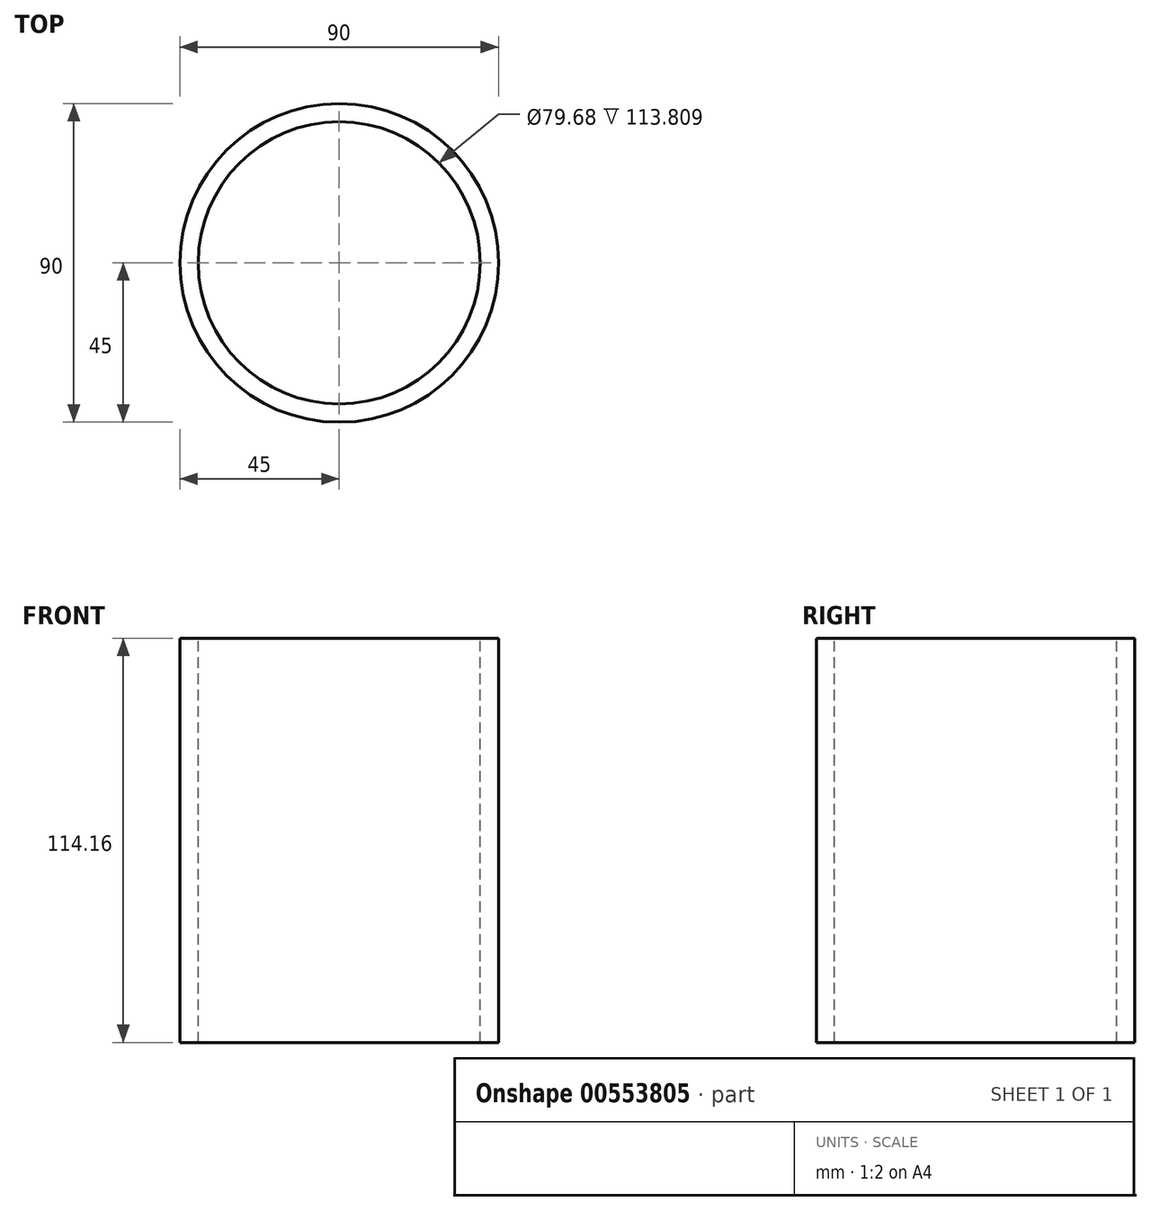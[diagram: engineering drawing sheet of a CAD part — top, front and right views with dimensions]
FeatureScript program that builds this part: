
annotation { "Feature Type Name" : "Feature", "Feature Type Description" : "" }
export const myFeature = defineFeature(function(context is Context, id is Id, definition is map)
    precondition{}
    {
        {
            var Q0;
            Q0=qCreatedBy(makeId("Front.planeOp"),FACE);
            var sketch = newSketch(context, id + "F0", { "sketchPlane" : qUnion([Q0])});
            skLineSegment(sketch, "E0", {"start": v(0, 32.92) * mm, "end": v(0, -87.08) * mm});
            skLineSegment(sketch, "E1", {"start": v(-70, -27.08) * mm, "end": v(70, -27.08) * mm});
            skLineSegment(sketch, "E2", {"start": v(-39.84, -27.08) * mm, "end": v(-39.84, 86.73) * mm});
            skLineSegment(sketch, "E3", {"start": v(-45, 86.73) * mm, "end": v(-45, -27.08) * mm});
            skLineSegment(sketch, "E4", {"start": v(-44.65, 87.08) * mm, "end": v(-40.2, 87.08) * mm});
            skArc(sketch, "E5", {"start": v(-44.65, 87.08) * mm, "mid": v(-44.9, 86.98) * mm, "end": v(-45, 86.73) * mm});
            skArc(sketch, "E6", {"start": v(-39.84, 86.73) * mm, "mid": v(-39.94, 86.98) * mm, "end": v(-40.2, 87.08) * mm});
            skLineSegment(sketch, "E7", {"start": v(-45, -27.08) * mm, "end": v(-39.84, -27.08) * mm});
            skSolve(sketch);
        }
        {
            var Q0;
            Q0=makeQuery(id+"F0.imprint","IMPRINT",FACE,{"disambiguationData":[TD([[makeQuery(id+"F0.imprint","IMPRINT",EDGE,{"derivedFrom":sQuery(id+"F0.wireOp",EDGE,"E2")}),1.0]])]});
            var Q1;
            Q1=sQuery(id+"F0.wireOp",EDGE,"E0");
            revolve(context, id + "F1", {"entities" : qUnion([Q0]), "axis" : qUnion([Q1]), "revolveType" : RevolveType.FULL});
        }
    });
